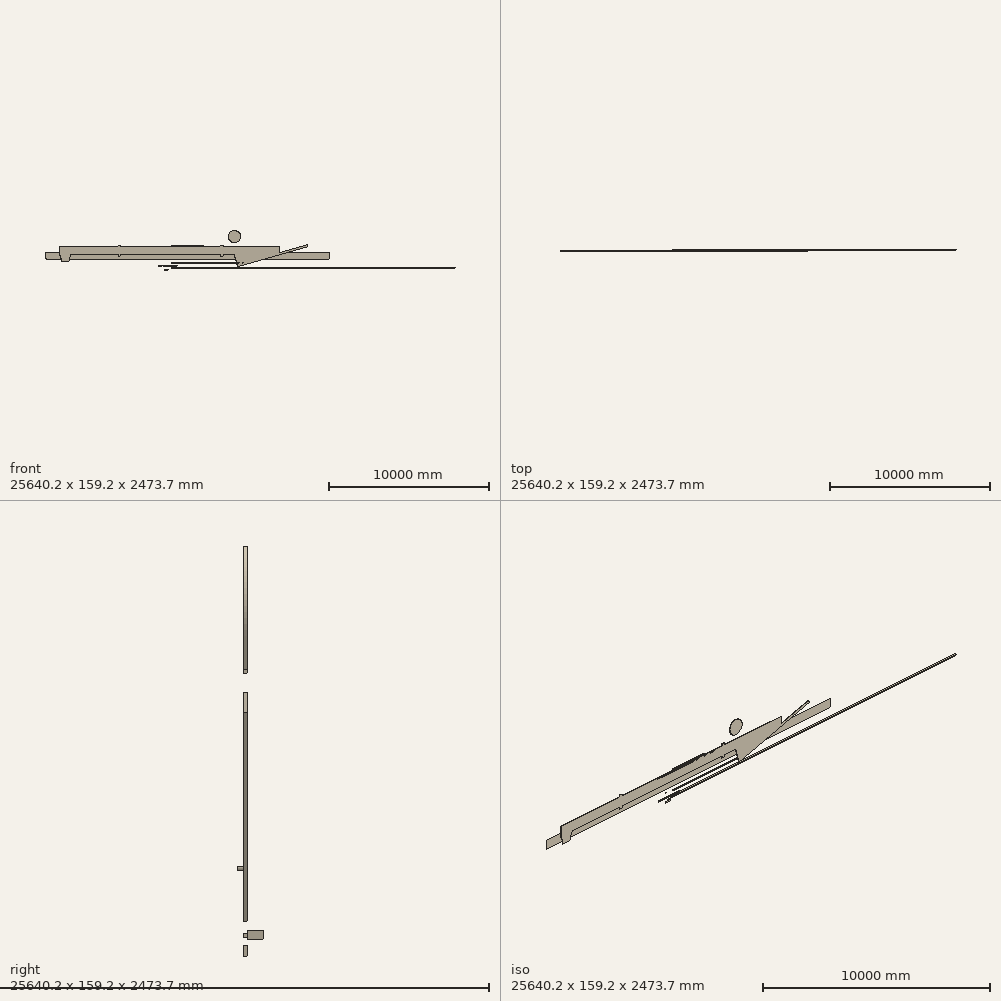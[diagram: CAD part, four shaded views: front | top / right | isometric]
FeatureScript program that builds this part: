
annotation { "Feature Type Name" : "Feature", "Feature Type Description" : "" }
export const myFeature = defineFeature(function(context is Context, id is Id, definition is map)
    precondition{}
    {
        {
            var Q0;
            Q0=qCreatedBy(makeId("Front.planeOp"),FACE);
            var sketch = newSketch(context, id + "F0", { "sketchPlane" : qUnion([Q0])});
            skLineSegment(sketch, "E0.bottom", {"start": v(-7994.64, 254) * mm, "end": v(-4337.04, 254) * mm});
            skLineSegment(sketch, "E0.top", {"start": v(-7994.64, -254) * mm, "end": v(-7990.84, -254) * mm});
            skLineSegment(sketch, "E0.left", {"start": v(-7994.64, 254) * mm, "end": v(-7994.64, -254) * mm});
            skPoint(sketch, "E0.middle", {"position": v(0, 0) * mm});
            skCircle(sketch, "E1", {"center": v(-3422.64, 0) * mm, "radius": 12.7 * mm});
            skCircle(sketch, "E2", {"center": v(2647.95, 0) * mm, "radius": 12.7 * mm});
            skCircle(sketch, "E3", {"center": v(-7969.24, 228.6) * mm, "radius": 12.7 * mm});
            skCircle(sketch, "E4", {"center": v(2139.95, 0) * mm, "radius": 12.7 * mm});
            skArc(sketch, "E5", {"start": v(-7400.14, -478.79) * mm, "mid": v(-7336.7, -374.26) * mm, "end": v(-7314.6, -254) * mm});
            skLineSegment(sketch, "E6.top", {"start": v(-7917.67, -699.17) * mm, "end": v(-7400.14, -699.17) * mm});
            skLineSegment(sketch, "E6.left", {"start": v(-7917.67, -464.07) * mm, "end": v(-7917.67, -699.17) * mm});
            skLineSegment(sketch, "E6.right", {"start": v(-7400.14, -464.07) * mm, "end": v(-7400.14, -699.17) * mm});
            skLineSegment(sketch, "E7.trimOffspring", {"start": v(-7314.6, -254) * mm, "end": v(-4337.04, -254) * mm});
            skArc(sketch, "E8.trimOffspring", {"start": v(-7990.84, -254) * mm, "mid": v(-7972.03, -365.22) * mm, "end": v(-7917.67, -464.07) * mm});
            skLineSegment(sketch, "E9.bottom", {"start": v(-4337.04, 355.6) * mm, "end": v(-4184.64, 355.6) * mm});
            skLineSegment(sketch, "E9.top", {"start": v(-4337.04, -355.6) * mm, "end": v(-4184.64, -355.6) * mm});
            skLineSegment(sketch, "E9.left", {"start": v(-4337.04, 355.6) * mm, "end": v(-4337.04, 254) * mm});
            skLineSegment(sketch, "E9.right", {"start": v(-4184.64, 355.6) * mm, "end": v(-4184.64, 254) * mm});
            skLineSegment(sketch, "E10.trimOffspring", {"start": v(-4337.04, -254) * mm, "end": v(-4337.04, -355.6) * mm});
            skLineSegment(sketch, "E11.trimOffspring", {"start": v(-4184.64, 254) * mm, "end": v(2063.76, 254) * mm});
            skLineSegment(sketch, "E12.trimOffspring", {"start": v(-4184.64, -254) * mm, "end": v(-4184.64, -355.6) * mm});
            skLineSegment(sketch, "E13.trimOffspring", {"start": v(-4184.64, -254) * mm, "end": v(2063.76, -254) * mm});
            skLineSegment(sketch, "E14.bottom", {"start": v(2063.76, 355.6) * mm, "end": v(2216.16, 355.6) * mm});
            skLineSegment(sketch, "E14.top", {"start": v(2063.76, -355.6) * mm, "end": v(2216.16, -355.6) * mm});
            skLineSegment(sketch, "E14.left", {"start": v(2063.76, 355.6) * mm, "end": v(2063.76, 254) * mm});
            skLineSegment(sketch, "E14.right", {"start": v(2216.16, 355.6) * mm, "end": v(2216.16, 254) * mm});
            skLineSegment(sketch, "E15.trimOffspring", {"start": v(2216.16, -254) * mm, "end": v(2912.87, -254) * mm});
            skLineSegment(sketch, "E16.trimOffspring", {"start": v(2063.76, -254) * mm, "end": v(2063.76, -355.6) * mm});
            skLineSegment(sketch, "E17.trimOffspring", {"start": v(2216.16, -254) * mm, "end": v(2216.16, -355.6) * mm});
            skLineSegment(sketch, "E18.0", {"start": v(7489.99, 370.7) * mm, "end": v(5772.15, -121.88) * mm});
            skLineSegment(sketch, "E19", {"start": v(7525, 248.62) * mm, "end": v(7489.99, 370.7) * mm});
            skLineSegment(sketch, "E20", {"start": v(5772.15, 248.62) * mm, "end": v(2216.16, 254) * mm});
            skLineSegment(sketch, "E21", {"start": v(5772.15, 248.62) * mm, "end": v(5772.15, -121.88) * mm});
            skLineSegment(sketch, "E22", {"start": v(7525, 248.62) * mm, "end": v(3130.1, -1011.6) * mm});
            skLineSegment(sketch, "E23", {"start": v(3130.1, -1011.6) * mm, "end": v(2912.87, -254) * mm});
            skCircle(sketch, "E24", {"center": v(3147.52, -980.18) * mm, "radius": 12.7 * mm});
            skCircle(sketch, "E25", {"center": v(2993.5, -443.03) * mm, "radius": 12.7 * mm});
            skSolve(sketch);
        }
        {
            var Q0;
            Q0=makeQuery(id+"F0.imprint","IMPRINT",FACE,{"disambiguationData":[TD([[makeQuery(id+"F0.imprint","IMPRINT",EDGE,{"derivedFrom":sQuery(id+"F0.wireOp",EDGE,"E0.bottom")}),-1.0]])]});
            extrude(context, id + "F1", {"entities" : qUnion([Q0]), "depth" : 25.4 * mm, "offsetDistance" : 25.4 * mm});
        }
        {
            var Q0;
            Q0=qCreatedBy(makeId("Front.planeOp"),FACE);
            var sketch = newSketch(context, id + "F2", { "sketchPlane" : qUnion([Q0])});
            skLineSegment(sketch, "E26.bottom", {"start": v(-2032, 224.2) * mm, "end": v(2032, 224.2) * mm});
            skLineSegment(sketch, "E26.top", {"start": v(-2032, 173.4) * mm, "end": v(2032, 173.4) * mm});
            skLineSegment(sketch, "E26.left", {"start": v(-2032, 224.2) * mm, "end": v(-2032, 173.4) * mm});
            skLineSegment(sketch, "E26.right", {"start": v(2032, 224.2) * mm, "end": v(2032, 173.4) * mm});
            skPoint(sketch, "E26.middle", {"position": v(0, 198.8) * mm});
            skCircle(sketch, "E27", {"center": v(-2006.6, 198.8) * mm, "radius": 12.7 * mm});
            skCircle(sketch, "E28", {"center": v(2006.6, 198.8) * mm, "radius": 12.7 * mm});
            skCircle(sketch, "E29", {"center": v(1701.8, 198.8) * mm, "radius": 12.7 * mm});
            skCircle(sketch, "E30", {"center": v(-1701.8, 198.8) * mm, "radius": 12.7 * mm});
            skSolve(sketch);
        }
        {
            var Q0;
            Q0=makeQuery(id+"F2.imprint","IMPRINT",FACE,{"disambiguationData":[TD([[makeQuery(id+"F2.imprint","IMPRINT",EDGE,{"derivedFrom":sQuery(id+"F2.wireOp",EDGE,"E26.bottom")}),-1.0]])]});
            extrude(context, id + "F3", {"entities" : qUnion([Q0]), "depth" : 25.4 * mm, "offsetDistance" : 25.4 * mm});
        }
        {
            var Q0;
            Q0=qCreatedBy(makeId("Front.planeOp"),FACE);
            var sketch = newSketch(context, id + "F4", { "sketchPlane" : qUnion([Q0])});
            skLineSegment(sketch, "E31.bottom", {"start": v(-1016, 330.2) * mm, "end": v(1016, 330.2) * mm});
            skLineSegment(sketch, "E31.top", {"start": v(-1016, 279.4) * mm, "end": v(1016, 279.4) * mm});
            skLineSegment(sketch, "E31.left", {"start": v(-1016, 330.2) * mm, "end": v(-1016, 279.4) * mm});
            skLineSegment(sketch, "E31.right", {"start": v(1016, 330.2) * mm, "end": v(1016, 279.4) * mm});
            skPoint(sketch, "E31.middle", {"position": v(0, 304.8) * mm});
            skCircle(sketch, "E32", {"center": v(990.6, 304.8) * mm, "radius": 12.7 * mm});
            skCircle(sketch, "E33", {"center": v(-990.6, 304.8) * mm, "radius": 12.7 * mm});
            skCircle(sketch, "E34", {"center": v(-685.8, 304.8) * mm, "radius": 12.7 * mm});
            skCircle(sketch, "E35", {"center": v(685.8, 304.8) * mm, "radius": 12.7 * mm});
            skSolve(sketch);
        }
        {
            var Q0;
            Q0=makeQuery(id+"F4.imprint","IMPRINT",FACE,{"disambiguationData":[TD([[makeQuery(id+"F4.imprint","IMPRINT",EDGE,{"derivedFrom":sQuery(id+"F4.wireOp",EDGE,"E31.bottom")}),-1.0]])]});
            extrude(context, id + "F5", {"entities" : qUnion([Q0]), "depth" : 25.4 * mm, "offsetDistance" : 25.4 * mm});
        }
        {
            var Q0;
            Q0=qCreatedBy(makeId("Front.planeOp"),FACE);
            var sketch = newSketch(context, id + "F6", { "sketchPlane" : qUnion([Q0])});
            skLineSegment(sketch, "E36.bottom", {"start": v(-8890, -539.97) * mm, "end": v(8890, -539.97) * mm});
            skLineSegment(sketch, "E36.top", {"start": v(-8890, -82.77) * mm, "end": v(8890, -82.77) * mm});
            skLineSegment(sketch, "E36.left", {"start": v(-8890, -539.97) * mm, "end": v(-8890, -82.77) * mm});
            skLineSegment(sketch, "E36.right", {"start": v(8890, -539.97) * mm, "end": v(8890, -82.77) * mm});
            skPoint(sketch, "E36.middle", {"position": v(0, -311.37) * mm});
            skCircle(sketch, "E37", {"center": v(-8864.6, -514.57) * mm, "radius": 12.7 * mm});
            skSolve(sketch);
        }
        {
            var Q0;
            Q0=makeQuery(id+"F6.imprint","IMPRINT",FACE,{"disambiguationData":[TD([[makeQuery(id+"F6.imprint","IMPRINT",EDGE,{"derivedFrom":sQuery(id+"F6.wireOp",EDGE,"E36.bottom")}),1.0]])]});
            extrude(context, id + "F7", {"entities" : qUnion([Q0]), "depth" : 3.17 * mm, "offsetDistance" : 25.4 * mm});
        }
        {
            var Q0;
            Q0=qCreatedBy(makeId("Front.planeOp"),FACE);
            var sketch = newSketch(context, id + "F8", { "sketchPlane" : qUnion([Q0])});
            skLineSegment(sketch, "E38.bottom", {"start": v(-999.05, -729.48) * mm, "end": v(3572.95, -729.48) * mm});
            skLineSegment(sketch, "E38.top", {"start": v(-999.05, -780.28) * mm, "end": v(3572.95, -780.28) * mm});
            skLineSegment(sketch, "E38.left", {"start": v(-999.05, -729.48) * mm, "end": v(-999.05, -780.28) * mm});
            skLineSegment(sketch, "E38.right", {"start": v(3572.95, -729.48) * mm, "end": v(3572.95, -780.28) * mm});
            skCircle(sketch, "E39", {"center": v(-948.25, -754.88) * mm, "radius": 12.7 * mm});
            skCircle(sketch, "E40", {"center": v(3522.15, -754.88) * mm, "radius": 12.7 * mm});
            skCircle(sketch, "E41", {"center": v(3217.35, -754.88) * mm, "radius": 12.7 * mm});
            skCircle(sketch, "E42", {"center": v(-643.45, -754.88) * mm, "radius": 12.7 * mm});
            skCircle(sketch, "E43", {"center": v(1185.35, -754.88) * mm, "radius": 12.7 * mm});
            skCircle(sketch, "E44", {"center": v(1388.55, -754.88) * mm, "radius": 12.7 * mm});
            skSolve(sketch);
        }
        {
            var Q0;
            Q0=makeQuery(id+"F8.imprint","IMPRINT",FACE,{"disambiguationData":[TD([[makeQuery(id+"F8.imprint","IMPRINT",EDGE,{"derivedFrom":sQuery(id+"F8.wireOp",EDGE,"E38.bottom")}),-1.0]])]});
            extrude(context, id + "F9", {"entities" : qUnion([Q0]), "depth" : 25.4 * mm, "offsetDistance" : 25.4 * mm});
        }
        {
            var Q0;
            Q0=qCreatedBy(makeId("Front.planeOp"),FACE);
            var sketch = newSketch(context, id + "F10", { "sketchPlane" : qUnion([Q0])});
            skLineSegment(sketch, "E45.bottom", {"start": v(-1878.38, -938.88) * mm, "end": v(-608.38, -938.88) * mm});
            skLineSegment(sketch, "E45.top", {"start": v(-1878.38, -989.68) * mm, "end": v(-608.38, -989.68) * mm});
            skLineSegment(sketch, "E45.left", {"start": v(-1878.38, -938.88) * mm, "end": v(-1878.38, -989.68) * mm});
            skLineSegment(sketch, "E45.right", {"start": v(-608.38, -938.88) * mm, "end": v(-608.38, -989.68) * mm});
            skPoint(sketch, "E45.middle", {"position": v(-1243.38, -964.28) * mm});
            skCircle(sketch, "E46", {"center": v(-633.78, -964.28) * mm, "radius": 12.7 * mm});
            skCircle(sketch, "E47", {"center": v(-1852.98, -964.28) * mm, "radius": 12.7 * mm});
            skCircle(sketch, "E48", {"center": v(-1548.18, -964.28) * mm, "radius": 12.7 * mm});
            skCircle(sketch, "E49", {"center": v(-938.58, -964.28) * mm, "radius": 12.7 * mm});
            skSolve(sketch);
        }
        {
            var Q0;
            Q0=makeQuery(id+"F10.imprint","IMPRINT",FACE,{"disambiguationData":[TD([[makeQuery(id+"F10.imprint","IMPRINT",EDGE,{"derivedFrom":sQuery(id+"F10.wireOp",EDGE,"E45.bottom")}),-1.0]])]});
            extrude(context, id + "F11", {"entities" : qUnion([Q0]), "depth" : 25.4 * mm, "offsetDistance" : 25.4 * mm});
        }
        {
            var Q0;
            Q0=qCreatedBy(makeId("Front.planeOp"),FACE);
            var sketch = newSketch(context, id + "F12", { "sketchPlane" : qUnion([Q0])});
            skCircle(sketch, "E50", {"center": v(-1433.9, -693.08) * mm, "radius": 12.7 * mm});
            skSolve(sketch);
        }
        {
            var Q0;
            Q0=makeQuery(id+"F12.imprint","IMPRINT",FACE,{"disambiguationData":[TD([[makeQuery(id+"F12.imprint","IMPRINT",EDGE,{"derivedFrom":sQuery(id+"F12.wireOp",EDGE,"E50")}),1.0]])]});
            extrude(context, id + "F13", {"entities" : qUnion([Q0]), "depth" : 63.5 * mm, "offsetDistance" : 25.4 * mm});
        }
        {
            var Q0;
            Q0=qCreatedBy(makeId("Front.planeOp"),FACE);
            var sketch = newSketch(context, id + "F14", { "sketchPlane" : qUnion([Q0])});
            skLineSegment(sketch, "E51.bottom", {"start": v(-1029.84, -1066.62) * mm, "end": v(16750.16, -1066.62) * mm});
            skLineSegment(sketch, "E51.top", {"start": v(-1029.84, -1117.42) * mm, "end": v(16750.16, -1117.42) * mm});
            skLineSegment(sketch, "E51.left", {"start": v(-1029.84, -1066.62) * mm, "end": v(-1029.84, -1117.42) * mm});
            skLineSegment(sketch, "E51.right", {"start": v(16750.16, -1066.62) * mm, "end": v(16750.16, -1117.42) * mm});
            skCircle(sketch, "E52", {"center": v(-991.74, -1092.02) * mm, "radius": 12.7 * mm});
            skCircle(sketch, "E53", {"center": v(16712.06, -1092.02) * mm, "radius": 12.7 * mm});
            skSolve(sketch);
        }
        {
            var Q0;
            Q0=makeQuery(id+"F14.imprint","IMPRINT",FACE,{"disambiguationData":[TD([[makeQuery(id+"F14.imprint","IMPRINT",EDGE,{"derivedFrom":sQuery(id+"F14.wireOp",EDGE,"E51.bottom")}),-1.0]])]});
            extrude(context, id + "F15", {"entities" : qUnion([Q0]), "oppositeDirection" : true, "depth" : 95.68 * mm, "offsetDistance" : 25.4 * mm});
        }
        {
            var Q0;
            Q0=qCreatedBy(makeId("Front.planeOp"),FACE);
            var sketch = newSketch(context, id + "F16", { "sketchPlane" : qUnion([Q0])});
            skLineSegment(sketch, "E54.bottom", {"start": v(-1351.83, -1085.24) * mm, "end": v(-1148.63, -1085.24) * mm});
            skLineSegment(sketch, "E54.top", {"start": v(-1351.83, -1110.64) * mm, "end": v(-1148.63, -1110.64) * mm});
            skLineSegment(sketch, "E54.left", {"start": v(-1351.83, -1085.24) * mm, "end": v(-1351.83, -1110.64) * mm});
            skLineSegment(sketch, "E54.right", {"start": v(-1148.63, -1085.24) * mm, "end": v(-1148.63, -1110.64) * mm});
            skSolve(sketch);
        }
        {
            var Q0;
            Q0=makeQuery(id+"F16.imprint","IMPRINT",FACE,{"disambiguationData":[TD([[makeQuery(id+"F16.imprint","IMPRINT",EDGE,{"derivedFrom":sQuery(id+"F16.wireOp",EDGE,"E54.bottom")}),-1.0]])]});
            extrude(context, id + "F17", {"entities" : qUnion([Q0]), "depth" : 25.4 * mm, "offsetDistance" : 25.4 * mm});
        }
        {
            var Q0;
            Q0=qCreatedBy(makeId("Front.planeOp"),FACE);
            var sketch = newSketch(context, id + "F18", { "sketchPlane" : qUnion([Q0])});
            skArc(sketch, "E55", {"start": v(3069.6, 511.91) * mm, "mid": v(2938.82, 1251.35) * mm, "end": v(2814.37, 510.82) * mm});
            skCircle(sketch, "E56", {"center": v(2940.45, 870.35) * mm, "radius": 12.7 * mm});
            skLineSegment(sketch, "E57.top", {"start": v(2814.37, 483.87) * mm, "end": v(3069.6, 483.87) * mm});
            skLineSegment(sketch, "E57.left", {"start": v(2814.37, 510.82) * mm, "end": v(2814.37, 483.87) * mm});
            skLineSegment(sketch, "E57.right", {"start": v(3069.6, 511.91) * mm, "end": v(3069.6, 483.87) * mm});
            skSolve(sketch);
        }
        {
            var Q0;
            Q0=makeQuery(id+"F18.imprint","IMPRINT",FACE,{"disambiguationData":[TD([[makeQuery(id+"F18.imprint","IMPRINT",EDGE,{"derivedFrom":sQuery(id+"F18.wireOp",EDGE,"E55")}),1.0]])]});
            extrude(context, id + "F19", {"entities" : qUnion([Q0]), "depth" : 25.4 * mm, "offsetDistance" : 25.4 * mm});
        }
        {
            var Q0;
            Q0=qCreatedBy(makeId("Front.planeOp"),FACE);
            var sketch = newSketch(context, id + "F20", { "sketchPlane" : qUnion([Q0])});
            skLineSegment(sketch, "E58.bottom", {"start": v(-1430.8, -1158.88) * mm, "end": v(-1176.8, -1158.88) * mm});
            skLineSegment(sketch, "E58.top", {"start": v(-1430.8, -1222.38) * mm, "end": v(-1176.8, -1222.38) * mm});
            skLineSegment(sketch, "E58.left", {"start": v(-1430.8, -1158.88) * mm, "end": v(-1430.8, -1222.38) * mm});
            skLineSegment(sketch, "E58.right", {"start": v(-1176.8, -1158.88) * mm, "end": v(-1176.8, -1222.38) * mm});
            skSolve(sketch);
        }
        {
            var Q0;
            Q0=makeQuery(id+"F20.imprint","IMPRINT",FACE,{"disambiguationData":[TD([[makeQuery(id+"F20.imprint","IMPRINT",EDGE,{"derivedFrom":sQuery(id+"F20.wireOp",EDGE,"E58.bottom")}),-1.0]])]});
            extrude(context, id + "F21", {"entities" : qUnion([Q0]), "depth" : 25.4 * mm, "offsetDistance" : 25.4 * mm});
        }
    });
